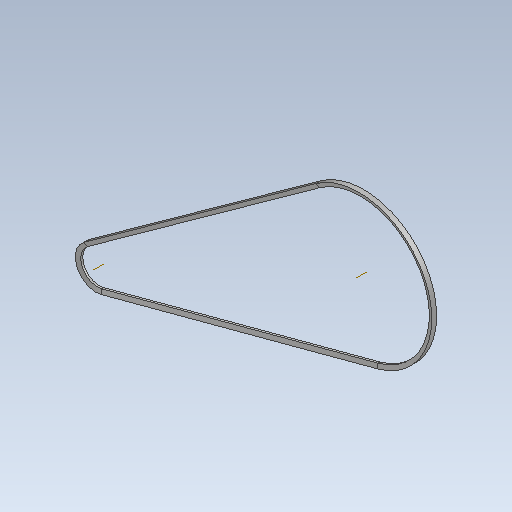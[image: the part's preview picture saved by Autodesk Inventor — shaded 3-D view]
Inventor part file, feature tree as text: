
AUTODESK INVENTOR PART (.ipt)
format: ipt  version: 2020.5 (Build 245400000, 400)  size: 98,304 bytes
history: native  units: mm (DEFAULTED — no unit token found)
features: other x5, sweep x1
ambient origin geometry x8: Origin, YZ Plane, XZ Plane, XY Plane, X Axis, Y Axis, Z Axis, Center Point
bodies: Solid1 (feature_tree)
feature tree (6):
  other  "Trayectoria de boceto"
  other  "Plano de sección transversal"
  other  "Eje de trabajo1"
  other  "Eje de trabajo2"
  sweep  "Correa"
  other  "Sección transversal"
